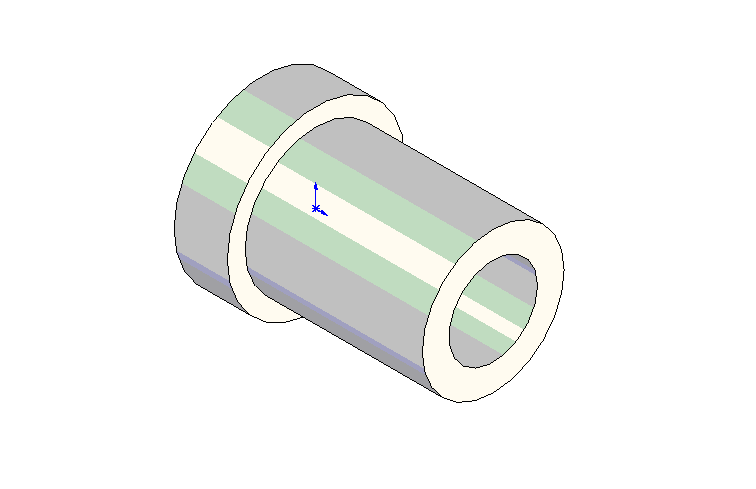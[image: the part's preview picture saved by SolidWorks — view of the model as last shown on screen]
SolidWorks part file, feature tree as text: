
SOLIDWORKS PART (.sldprt)
format: sldprt  version: not decoded by parser v0  size: 159,232 bytes
history: native  units: mm
features: sketch x4, plane x3, extrude x2, cut_extrude x2, material x1 (+10 scaffold rows collapsed)
feature tree (22):
  scaffold x10  (default folders/planes/origin — collapsed)
  material  "Matériau <non spécifié>"
  plane  "Plan de face"
  plane  "Plan de dessus"
  plane  "Plan de droite"
  sketch  "Esquisse1"  dims[D1=8.0mm]
  extrude  "Extrusion1"  Depth=10mm
  sketch  "Esquisse2"  dims[D1=10.0mm]
  extrude  "Extrusion2"  [1 undecoded]
  sketch  "Esquisse3"  dims[D1=5.0mm]
  cut_extrude  "Enlèv. mat.-Extru.1"  Depth=3mm
  sketch  "Esquisse4"  dims[D1=5.0mm]
  cut_extrude  "Enlèv. mat.-Extru.2"  [1 undecoded]
decode coverage: 6 of 8 modeling features carry decoded parameters
note: 2 parameter values undecoded
note: suppression state not decoded; provenance and decode notes live in map.json
